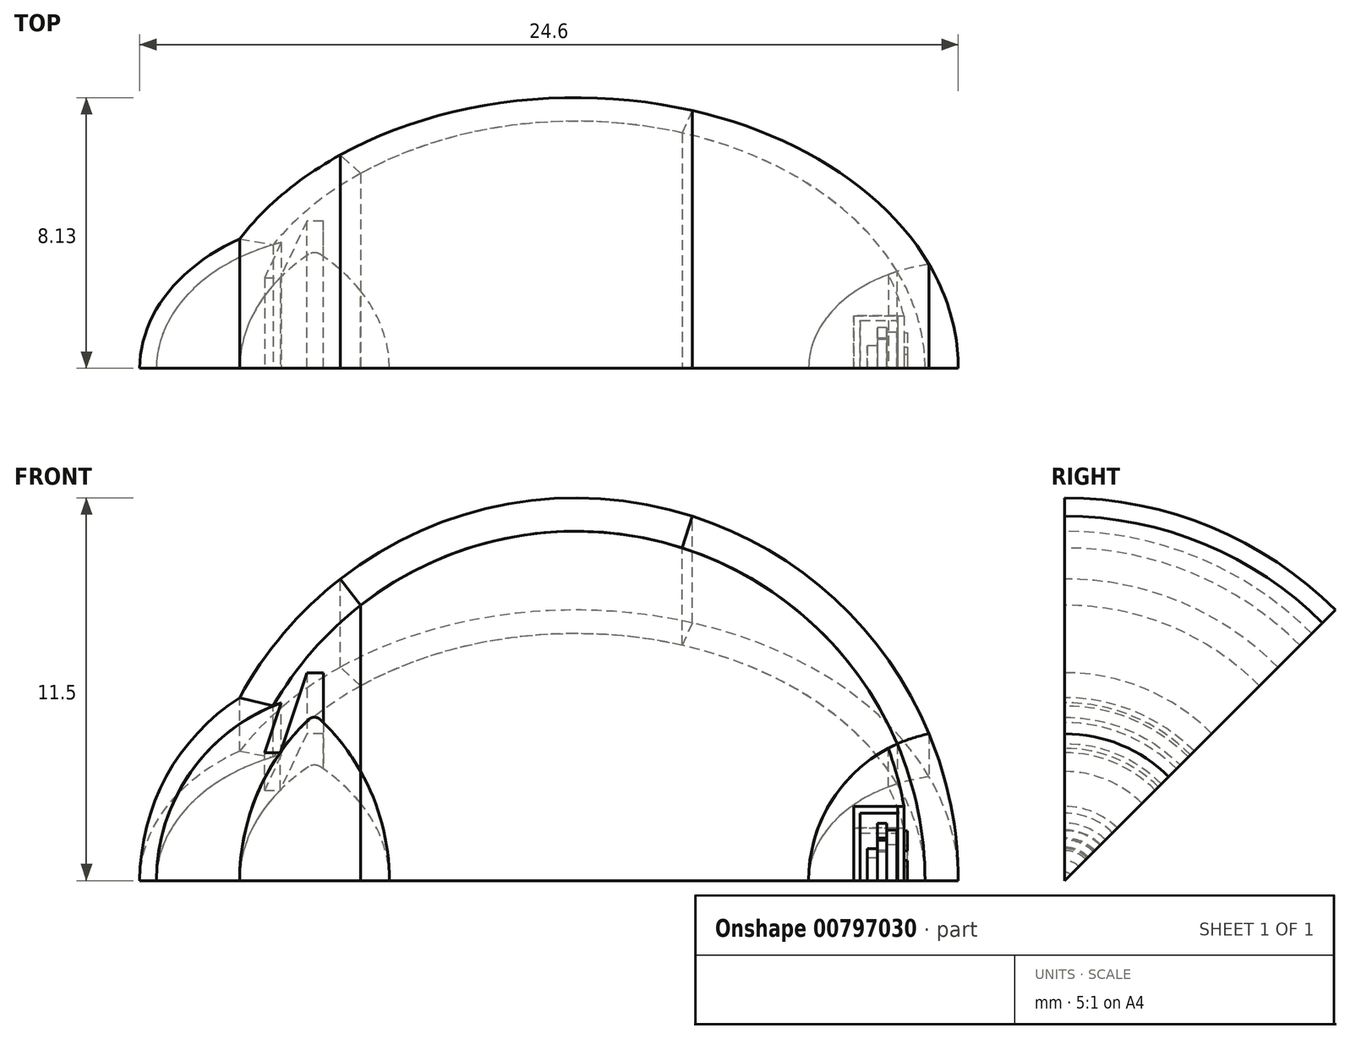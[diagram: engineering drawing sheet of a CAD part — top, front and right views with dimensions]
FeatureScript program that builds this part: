
annotation { "Feature Type Name" : "Feature", "Feature Type Description" : "" }
export const myFeature = defineFeature(function(context is Context, id is Id, definition is map)
    precondition{}
    {
        {
            var Q0;
            Q0=qCreatedBy(makeId("Front.planeOp"),FACE);
            var sketch = newSketch(context, id + "F0", { "sketchPlane" : qUnion([Q0])});
            skArc(sketch, "E0", {"start": v(11.5, 0) * mm, "mid": v(2.84, 11.14) * mm, "end": v(-10.1, 5.5) * mm});
            skLineSegment(sketch, "E1", {"start": v(11.5, 0) * mm, "end": v(-11.5, 0) * mm});
            skArc(sketch, "E2", {"start": v(-10.1, 5.5) * mm, "mid": v(-12.3, 3.13) * mm, "end": v(-13.1, 0) * mm});
            skLineSegment(sketch, "E3", {"start": v(-11.5, 0) * mm, "end": v(-13.1, 0) * mm});
            skSolve(sketch);
        }
        {
            var Q0;
            Q0=qSketchRegion(id+"F0",true);
            var Q1;
            Q1=sQuery(id+"F0.wireOp",EDGE,"E1");
            revolve(context, id + "F1", {"entities" : qUnion([Q0]), "axis" : qUnion([Q1]), "revolveType" : RevolveType.ONE_DIRECTION, "angle" : 45 * degree});
        }
        {
            var Q0;
            Q0=qCreatedBy(makeId("Front.planeOp"),FACE);
            var sketch = newSketch(context, id + "F2", { "sketchPlane" : qUnion([Q0])});
            skLineSegment(sketch, "E4", {"start": v(-10.1, 5.5) * mm, "end": v(-9.1, 5.25) * mm});
            skLineSegment(sketch, "E5", {"start": v(11.5, 0) * mm, "end": v(10.5, 0) * mm});
            skArc(sketch, "E6", {"start": v(10.5, 0) * mm, "mid": v(2.72, 10.14) * mm, "end": v(-9.1, 5.25) * mm});
            skArc(sketch, "E7", {"start": v(11.5, 0) * mm, "mid": v(2.84, 11.14) * mm, "end": v(-10.1, 5.5) * mm});
            skSolve(sketch);
        }
        {
            var Q0;
            Q0=makeQuery(id+"F2.imprint","IMPRINT",FACE,{"disambiguationData":[TD([[makeQuery(id+"F2.imprint","IMPRINT",EDGE,{"derivedFrom":sQuery(id+"F2.wireOp",EDGE,"E4")}),1.0]])]});
            var Q1;
            Q1=sQuery(id+"F2.wireOp",EDGE,"E6");
            var Q2;
            Q2=sQuery(id+"F2.wireOp",EDGE,"E4");
            var Q3;
            Q3=sQuery(id+"F0.wireOp",EDGE,"E1");
            revolve(context, id + "F3", {"operationType" : NewBodyOperationType.REMOVE, "entities" : qUnion([Q0]), "surfaceEntities" : qUnion([Q1, Q2]), "axis" : qUnion([Q3]), "revolveType" : RevolveType.ONE_DIRECTION, "angle" : 45 * degree});
        }
        {
            var Q0;
            Q0=qSketchRegion(id+"F2",true);
            var Q1;
            Q1=sQuery(id+"F0.wireOp",EDGE,"E1");
            revolve(context, id + "F4", {"entities" : qUnion([Q0]), "axis" : qUnion([Q1]), "revolveType" : RevolveType.ONE_DIRECTION, "angle" : 45 * degree});
        }
        {
            var Q0;
            Q0=makeQuery(id+"F0.imprint","IMPRINT",FACE,{"disambiguationData":[TD([[makeQuery(id+"F0.imprint","IMPRINT",EDGE,{"derivedFrom":sQuery(id+"F0.wireOp",EDGE,"E0")}),1.0]])]});
            var sketch = newSketch(context, id + "F5", { "sketchPlane" : qUnion([Q0])});
            skArc(sketch, "E8", {"start": v(-9.1, 5.25) * mm, "mid": v(-11.64, 3.16) * mm, "end": v(-12.6, 0) * mm});
            skLineSegment(sketch, "E9", {"start": v(-10.1, 5.5) * mm, "end": v(-9.1, 5.25) * mm});
            skLineSegment(sketch, "E10", {"start": v(-13.1, 0) * mm, "end": v(-12.6, 0) * mm});
            skArc(sketch, "E11", {"start": v(-10.1, 5.5) * mm, "mid": v(-12.3, 3.13) * mm, "end": v(-13.1, 0) * mm});
            skSolve(sketch);
        }
        {
            var Q0;
            Q0=qSketchRegion(id+"F5",true);
            var Q1;
            Q1=sQuery(id+"F5.wireOp",EDGE,"E8");
            var Q2;
            Q2=sQuery(id+"F5.wireOp",EDGE,"E9");
            var Q3;
            Q3=sQuery(id+"F0.wireOp",EDGE,"E3");
            revolve(context, id + "F6", {"operationType" : NewBodyOperationType.REMOVE, "entities" : qUnion([Q0]), "surfaceEntities" : qUnion([Q1, Q2]), "axis" : qUnion([Q3]), "revolveType" : RevolveType.ONE_DIRECTION, "angle" : 45 * degree});
        }
        {
            var Q0;
            Q0=qSketchRegion(id+"F5",true);
            var Q1;
            Q1=sQuery(id+"F0.wireOp",EDGE,"E1");
            revolve(context, id + "F7", {"entities" : qUnion([Q0]), "axis" : qUnion([Q1]), "revolveType" : RevolveType.ONE_DIRECTION, "angle" : 45 * degree});
        }
        {
            var Q0;
            Q0=qCreatedBy(makeId("Front.planeOp"),FACE);
            var sketch = newSketch(context, id + "F8", { "sketchPlane" : qUnion([Q0])});
            skArc(sketch, "E12", {"start": v(10, 0) * mm, "mid": v(8.28, 6.14) * mm, "end": v(3.2, 10) * mm});
            skLineSegment(sketch, "E13", {"start": v(10, 0) * mm, "end": v(10.5, 0) * mm});
            skArc(sketch, "E14", {"start": v(10.5, 0) * mm, "mid": v(8.48, 6.2) * mm, "end": v(3.2, 10) * mm});
            skSolve(sketch);
        }
        {
            var Q0;
            Q0=qSketchRegion(id+"F8",true);
            var Q1;
            Q1=sQuery(id+"F8.wireOp",EDGE,"E12");
            var Q2;
            Q2=sQuery(id+"F0.wireOp",EDGE,"E1");
            revolve(context, id + "F9", {"operationType" : NewBodyOperationType.REMOVE, "entities" : qUnion([Q0]), "surfaceEntities" : qUnion([Q1]), "axis" : qUnion([Q2]), "revolveType" : RevolveType.ONE_DIRECTION, "angle" : 45 * degree});
        }
        {
            var Q0;
            Q0=qSketchRegion(id+"F8",true);
            var Q1;
            Q1=sQuery(id+"F8.wireOp",EDGE,"E13");
            revolve(context, id + "F10", {"surfaceOperationType" : NewSurfaceOperationType.NEW, "entities" : qUnion([Q0]), "axis" : qUnion([Q1]), "revolveType" : RevolveType.ONE_DIRECTION, "oppositeDirection" : true, "angle" : 45 * degree});
        }
        {
            var Q0;
            Q0=makeQuery(id+"F0.imprint","IMPRINT",FACE,{"disambiguationData":[TD([[makeQuery(id+"F0.imprint","IMPRINT",EDGE,{"derivedFrom":sQuery(id+"F0.wireOp",EDGE,"E0")}),1.0]])]});
            var sketch = newSketch(context, id + "F11", { "sketchPlane" : qUnion([Q0])});
            skLineSegment(sketch, "E15", {"start": v(8.35, 0) * mm, "end": v(9.86, 0) * mm});
            skLineSegment(sketch, "E16", {"start": v(9.86, 0) * mm, "end": v(9.86, 2.23) * mm});
            skLineSegment(sketch, "E17", {"start": v(9.86, 2.23) * mm, "end": v(8.35, 2.23) * mm});
            skLineSegment(sketch, "E18", {"start": v(8.35, 2.23) * mm, "end": v(8.35, 0) * mm});
            skSolve(sketch);
        }
        {
            var Q0;
            Q0=qSketchRegion(id+"F11",true);
            var Q1;
            Q1=sQuery(id+"F11.wireOp",EDGE,"E15");
            revolve(context, id + "F12", {"operationType" : NewBodyOperationType.REMOVE, "entities" : qUnion([Q0]), "axis" : qUnion([Q1]), "revolveType" : RevolveType.ONE_DIRECTION, "oppositeDirection" : true, "angle" : 45 * degree});
        }
        {
            var Q0;
            Q0=qSketchRegion(id+"F11",true);
            var Q1;
            Q1=sQuery(id+"F0.wireOp",EDGE,"E1");
            revolve(context, id + "F13", {"entities" : qUnion([Q0]), "axis" : qUnion([Q1]), "revolveType" : RevolveType.ONE_DIRECTION, "angle" : 45 * degree});
        }
        {
            var Q0;
            Q0=qCreatedBy(makeId("Front.planeOp"),FACE);
            var sketch = newSketch(context, id + "F14", { "sketchPlane" : qUnion([Q0])});
            skLineSegment(sketch, "E19", {"start": v(9.86, 2.23) * mm, "end": v(9.86, 0) * mm});
            skLineSegment(sketch, "E20", {"start": v(9.86, 0) * mm, "end": v(10, 0) * mm});
            skArc(sketch, "E21", {"start": v(10, 0) * mm, "mid": v(10, 1.12) * mm, "end": v(9.86, 2.23) * mm});
            skSolve(sketch);
        }
        {
            var Q0;
            Q0=qSketchRegion(id+"F14",true);
            var Q1;
            Q1=sQuery(id+"F14.wireOp",EDGE,"E20");
            revolve(context, id + "F15", {"operationType" : NewBodyOperationType.REMOVE, "entities" : qUnion([Q0]), "axis" : qUnion([Q1]), "revolveType" : RevolveType.ONE_DIRECTION, "oppositeDirection" : true, "angle" : 45 * degree});
        }
        {
            var Q0;
            Q0=qSketchRegion(id+"F14",true);
            var Q1;
            Q1=sQuery(id+"F0.wireOp",EDGE,"E1");
            revolve(context, id + "F16", {"operationType" : NewBodyOperationType.ADD, "entities" : qUnion([Q0]), "axis" : qUnion([Q1]), "revolveType" : RevolveType.ONE_DIRECTION, "angle" : 45 * degree});
        }
        {
            var Q0;
            Q0=qCreatedBy(makeId("Front.planeOp"),FACE);
            var sketch = newSketch(context, id + "F17", { "sketchPlane" : qUnion([Q0])});
            skLineSegment(sketch, "E22", {"start": v(3.5, 10.95) * mm, "end": v(3.2, 10) * mm});
            skArc(sketch, "E23", {"start": v(10.5, 0) * mm, "mid": v(8.48, 6.2) * mm, "end": v(3.2, 10) * mm});
            skArc(sketch, "E24", {"start": v(11.5, 0) * mm, "mid": v(9.29, 6.78) * mm, "end": v(3.5, 10.95) * mm});
            skLineSegment(sketch, "E25", {"start": v(10.5, 0) * mm, "end": v(11.5, 0) * mm});
            skSolve(sketch);
        }
        {
            var Q0;
            Q0=qSketchRegion(id+"F17",true);
            var Q1;
            Q1=sQuery(id+"F17.wireOp",EDGE,"E25");
            revolve(context, id + "F18", {"operationType" : NewBodyOperationType.REMOVE, "entities" : qUnion([Q0]), "axis" : qUnion([Q1]), "revolveType" : RevolveType.FULL, "oppositeDirection" : true});
        }
        {
            var Q0;
            Q0=qSketchRegion(id+"F17",true);
            var Q1;
            Q1=sQuery(id+"F0.wireOp",EDGE,"E1");
            revolve(context, id + "F19", {"entities" : qUnion([Q0]), "axis" : qUnion([Q1]), "revolveType" : RevolveType.ONE_DIRECTION, "angle" : 45 * degree});
        }
        {
            var Q0;
            Q0=qCreatedBy(makeId("Front.planeOp"),FACE);
            var sketch = newSketch(context, id + "F20", { "sketchPlane" : qUnion([Q0])});
            skArc(sketch, "E26", {"start": v(-8.85, 5.34) * mm, "mid": v(-11.57, 3.26) * mm, "end": v(-12.6, 0) * mm});
            skLineSegment(sketch, "E27", {"start": v(-8.85, 5.34) * mm, "end": v(-9.35, 3.84) * mm});
            skLineSegment(sketch, "E28", {"start": v(-9.35, 3.84) * mm, "end": v(-8.85, 3.84) * mm});
            skLineSegment(sketch, "E29", {"start": v(-12.6, 0) * mm, "end": v(-8.85, 0) * mm});
            skLineSegment(sketch, "E30", {"start": v(-8.85, 3.84) * mm, "end": v(-8.85, 0) * mm});
            skSolve(sketch);
        }
        {
            var Q0;
            Q0=qSketchRegion(id+"F20",true);
            var Q1;
            Q1=sQuery(id+"F20.wireOp",EDGE,"E29");
            revolve(context, id + "F21", {"operationType" : NewBodyOperationType.REMOVE, "entities" : qUnion([Q0]), "axis" : qUnion([Q1]), "revolveType" : RevolveType.FULL, "oppositeDirection" : true});
        }
        {
            var Q0;
            Q0=qSketchRegion(id+"F20",true);
            var Q1;
            Q1=sQuery(id+"F0.wireOp",EDGE,"E1");
            revolve(context, id + "F22", {"entities" : qUnion([Q0]), "axis" : qUnion([Q1]), "revolveType" : RevolveType.ONE_DIRECTION, "angle" : 45 * degree});
        }
        {
            var Q0;
            Q0=qCreatedBy(makeId("Front.planeOp"),FACE);
            var sketch = newSketch(context, id + "F23", { "sketchPlane" : qUnion([Q0])});
            skLineSegment(sketch, "E31", {"start": v(-5.6, 0) * mm, "end": v(-10.1, 0) * mm});
            skArc(sketch, "E32", {"start": v(-8.02, 4.84) * mm, "mid": v(-9.56, 2.63) * mm, "end": v(-10.1, 0) * mm});
            skLineSegment(sketch, "E33", {"start": v(-8.1, 0) * mm, "end": v(-8.1, 4.77) * mm, "construction": true});
            skArc(sketch, "E34", {"start": v(-5.6, 0) * mm, "mid": v(-6.14, 2.63) * mm, "end": v(-7.68, 4.84) * mm});
            skPoint(sketch, "E35.visualSharp", {"position": v(-7.85, 5) * mm});
            skArc(sketch, "E35.filletArc", {"start": v(-7.68, 4.84) * mm, "mid": v(-7.85, 4.91) * mm, "end": v(-8.02, 4.84) * mm});
            skSolve(sketch);
        }
        {
            var Q0;
            Q0=qSketchRegion(id+"F23",true);
            var Q1;
            Q1=sQuery(id+"F0.wireOp",EDGE,"E1");
            revolve(context, id + "F24", {"operationType" : NewBodyOperationType.REMOVE, "entities" : qUnion([Q0]), "axis" : qUnion([Q1]), "revolveType" : RevolveType.FULL, "oppositeDirection" : true});
        }
        {
            var Q0;
            Q0=qSketchRegion(id+"F23",true);
            var Q1;
            Q1=sQuery(id+"F0.wireOp",EDGE,"E1");
            revolve(context, id + "F25", {"entities" : qUnion([Q0]), "axis" : qUnion([Q1]), "revolveType" : RevolveType.ONE_DIRECTION, "angle" : 45 * degree});
        }
        {
            var Q0;
            Q0=qCreatedBy(makeId("Front.planeOp"),FACE);
            var sketch = newSketch(context, id + "F26", { "sketchPlane" : qUnion([Q0])});
            skLineSegment(sketch, "E36", {"start": v(-9.35, 3.84) * mm, "end": v(-8.88, 3.84) * mm});
            skLineSegment(sketch, "E37", {"start": v(-8.88, 3.84) * mm, "end": v(-8.08, 6.25) * mm});
            skLineSegment(sketch, "E38", {"start": v(-8.08, 6.25) * mm, "end": v(-7.58, 6.25) * mm});
            skLineSegment(sketch, "E39", {"start": v(-7.58, 6.25) * mm, "end": v(-7.58, 4.75) * mm});
            skLineSegment(sketch, "E40", {"start": v(-6.46, 3.28) * mm, "end": v(-6.46, 8.28) * mm});
            skLineSegment(sketch, "E41", {"start": v(-9.35, 3.84) * mm, "end": v(-8.85, 5.34) * mm});
            skArc(sketch, "E42", {"start": v(-6.46, 8.28) * mm, "mid": v(-7.92, 6.9) * mm, "end": v(-9.1, 5.25) * mm});
            skArc(sketch, "E43", {"start": v(-8.85, 5.34) * mm, "mid": v(-8.97, 5.3) * mm, "end": v(-9.1, 5.25) * mm});
            skArc(sketch, "E44", {"start": v(-6.46, 3.28) * mm, "mid": v(-6.97, 4.05) * mm, "end": v(-7.58, 4.75) * mm});
            skSolve(sketch);
        }
        {
            var Q0;
            Q0=qSketchRegion(id+"F26",true);
            var Q1;
            Q1=sQuery(id+"F23.wireOp",EDGE,"E31");
            revolve(context, id + "F27", {"operationType" : NewBodyOperationType.REMOVE, "entities" : qUnion([Q0]), "axis" : qUnion([Q1]), "revolveType" : RevolveType.FULL, "oppositeDirection" : true});
        }
        {
            var Q0;
            Q0=qSketchRegion(id+"F26",true);
            var Q1;
            Q1=sQuery(id+"F23.wireOp",EDGE,"E31");
            revolve(context, id + "F28", {"entities" : qUnion([Q0]), "axis" : qUnion([Q1]), "revolveType" : RevolveType.ONE_DIRECTION, "angle" : 45 * degree});
        }
        {
            var Q0;
            Q0=qCreatedBy(makeId("Front.planeOp"),FACE);
            var sketch = newSketch(context, id + "F29", { "sketchPlane" : qUnion([Q0])});
            skLineSegment(sketch, "E45", {"start": v(-6.46, 8.28) * mm, "end": v(-7.07, 9.07) * mm});
            skArc(sketch, "E46", {"start": v(-7.07, 9.07) * mm, "mid": v(-8.77, 7.44) * mm, "end": v(-10.1, 5.5) * mm});
            skArc(sketch, "E47", {"start": v(-6.46, 8.28) * mm, "mid": v(-7.92, 6.9) * mm, "end": v(-9.1, 5.25) * mm});
            skPoint(sketch, "E47.second.point", {"position": v(-9.1, 5.25) * mm});
            skPoint(sketch, "E47.third.point", {"position": v(-6.46, 8.28) * mm});
            skLineSegment(sketch, "E48", {"start": v(-10.1, 5.5) * mm, "end": v(-9.1, 5.25) * mm});
            skSolve(sketch);
        }
        {
            var Q0;
            Q0=qSketchRegion(id+"F29",true);
            var Q1;
            Q1=sQuery(id+"F23.wireOp",EDGE,"E31");
            revolve(context, id + "F30", {"operationType" : NewBodyOperationType.REMOVE, "entities" : qUnion([Q0]), "axis" : qUnion([Q1]), "revolveType" : RevolveType.FULL, "oppositeDirection" : true});
        }
        {
            var Q0;
            Q0=qSketchRegion(id+"F29",true);
            var Q1;
            Q1=sQuery(id+"F23.wireOp",EDGE,"E31");
            revolve(context, id + "F31", {"entities" : qUnion([Q0]), "axis" : qUnion([Q1]), "revolveType" : RevolveType.ONE_DIRECTION, "angle" : 45 * degree});
        }
        {
            var Q0;
            Q0=qCreatedBy(makeId("Front.planeOp"),FACE);
            var sketch = newSketch(context, id + "F32", { "sketchPlane" : qUnion([Q0])});
            skLineSegment(sketch, "E49", {"start": v(-6.46, 0) * mm, "end": v(-5.6, 0) * mm});
            skLineSegment(sketch, "E50", {"start": v(-6.46, 0) * mm, "end": v(-6.46, 3.28) * mm});
            skArc(sketch, "E51", {"start": v(-5.6, 0) * mm, "mid": v(-5.82, 1.7) * mm, "end": v(-6.46, 3.28) * mm});
            skPoint(sketch, "E51.third.point", {"position": v(-5.6, 0) * mm});
            skSolve(sketch);
        }
        {
            var Q0;
            Q0=qSketchRegion(id+"F32",true);
            var Q1;
            Q1=sQuery(id+"F32.wireOp",EDGE,"E49");
            revolve(context, id + "F33", {"operationType" : NewBodyOperationType.REMOVE, "entities" : qUnion([Q0]), "axis" : qUnion([Q1]), "revolveType" : RevolveType.FULL, "oppositeDirection" : true});
        }
        {
            var Q0;
            Q0=qSketchRegion(id+"F32",true);
            var Q1;
            Q1=sQuery(id+"F23.wireOp",EDGE,"E31");
            revolve(context, id + "F34", {"entities" : qUnion([Q0]), "axis" : qUnion([Q1]), "revolveType" : RevolveType.ONE_DIRECTION, "angle" : 45 * degree});
        }
        {
            var Q0;
            Q0=makeQuery(id+"F0.imprint","IMPRINT",FACE,{"disambiguationData":[TD([[makeQuery(id+"F0.imprint","IMPRINT",EDGE,{"derivedFrom":sQuery(id+"F0.wireOp",EDGE,"E0")}),1.0]])]});
            var sketch = newSketch(context, id + "F35", { "sketchPlane" : qUnion([Q0])});
            skLineSegment(sketch, "E52", {"start": v(9.67, 0) * mm, "end": v(9.67, 2.23) * mm});
            skLineSegment(sketch, "E53", {"start": v(9.67, 2.23) * mm, "end": v(9.86, 2.23) * mm});
            skLineSegment(sketch, "E54", {"start": v(9.86, 2.23) * mm, "end": v(9.86, 0) * mm});
            skSolve(sketch);
        }
        {
            var Q0;
            {var subQ0=sQuery(id+"F35.wireOp",EDGE,"E52");Q0=makeQuery(id+"F35.imprint","IMPRINT",FACE,{"disambiguationData":[TD([[makeQuery(id+"F35.imprint","IMPRINT",EDGE,{"derivedFrom":subQ0}),-1.0]])]});}
            var Q1;
            Q1=sQuery(id+"F0.wireOp",EDGE,"E1");
            revolve(context, id + "F36", {"operationType" : NewBodyOperationType.REMOVE, "surfaceOperationType" : NewSurfaceOperationType.NEW, "entities" : qUnion([Q0]), "axis" : qUnion([Q1]), "revolveType" : RevolveType.ONE_DIRECTION, "angle" : 45 * degree});
        }
        {
            var Q0;
            Q0=makeQuery(id+"F0.imprint","IMPRINT",FACE,{"disambiguationData":[TD([[makeQuery(id+"F0.imprint","IMPRINT",EDGE,{"derivedFrom":sQuery(id+"F0.wireOp",EDGE,"E0")}),1.0]])]});
            var sketch = newSketch(context, id + "F37", { "sketchPlane" : qUnion([Q0])});
            skLineSegment(sketch, "E55.bottom", {"start": v(9.67, 2.23) * mm, "end": v(9.86, 2.23) * mm});
            skLineSegment(sketch, "E55.top", {"start": v(9.67, 0) * mm, "end": v(9.86, 0) * mm});
            skLineSegment(sketch, "E55.left", {"start": v(9.67, 2.23) * mm, "end": v(9.67, 0) * mm});
            skLineSegment(sketch, "E55.right", {"start": v(9.86, 2.23) * mm, "end": v(9.86, 0) * mm});
            skSolve(sketch);
        }
        {
            var Q0;
            Q0 = qSketchRegion(id + "F37", true);
            var Q1;
            Q1=sQuery(id+"F0.wireOp",EDGE,"E1");
            revolve(context, id + "F38", {"surfaceOperationType" : NewSurfaceOperationType.NEW, "entities" : qUnion([Q0]), "axis" : qUnion([Q1]), "revolveType" : RevolveType.ONE_DIRECTION, "angle" : 45 * degree});
        }
        {
            var Q0;
            Q0=makeQuery(id+"F0.imprint","IMPRINT",FACE,{"disambiguationData":[TD([[makeQuery(id+"F0.imprint","IMPRINT",EDGE,{"derivedFrom":sQuery(id+"F0.wireOp",EDGE,"E0")}),1.0]])]});
            var sketch = newSketch(context, id + "F39", { "sketchPlane" : qUnion([Q0])});
            skLineSegment(sketch, "E56", {"start": v(8.55, 0) * mm, "end": v(8.55, 2.03) * mm});
            skLineSegment(sketch, "E57", {"start": v(8.55, 2.03) * mm, "end": v(9.67, 2.03) * mm});
            skLineSegment(sketch, "E58", {"start": v(9.67, 2.03) * mm, "end": v(9.67, 2.23) * mm});
            skLineSegment(sketch, "E59", {"start": v(9.67, 2.23) * mm, "end": v(8.35, 2.23) * mm});
            skLineSegment(sketch, "E60", {"start": v(8.35, 2.23) * mm, "end": v(8.35, 0) * mm});
            skLineSegment(sketch, "E61", {"start": v(8.35, 0) * mm, "end": v(8.55, 0) * mm});
            skSolve(sketch);
        }
        {
            var Q0;
            Q0 = qSketchRegion(id + "F39", true);
            var Q1;
            Q1=sQuery(id+"F0.wireOp",EDGE,"E1");
            revolve(context, id + "F40", {"operationType" : NewBodyOperationType.REMOVE, "surfaceOperationType" : NewSurfaceOperationType.NEW, "entities" : qUnion([Q0]), "axis" : qUnion([Q1]), "revolveType" : RevolveType.ONE_DIRECTION, "angle" : 45 * degree});
        }
        {
            var Q0;
            Q0 = qSketchRegion(id + "F39", true);
            var Q1;
            Q1=sQuery(id+"F0.wireOp",EDGE,"E1");
            revolve(context, id + "F41", {"surfaceOperationType" : NewSurfaceOperationType.NEW, "entities" : qUnion([Q0]), "axis" : qUnion([Q1]), "revolveType" : RevolveType.ONE_DIRECTION, "angle" : 45 * degree});
        }
        {
            var Q0;
            Q0=makeQuery(id+"F0.imprint","IMPRINT",FACE,{"disambiguationData":[TD([[makeQuery(id+"F0.imprint","IMPRINT",EDGE,{"derivedFrom":sQuery(id+"F0.wireOp",EDGE,"E0")}),1.0]])]});
            var sketch = newSketch(context, id + "F42", { "sketchPlane" : qUnion([Q0])});
            skLineSegment(sketch, "E62.bottom", {"start": v(9.65, 0) * mm, "end": v(9.35, 0) * mm});
            skLineSegment(sketch, "E62.top", {"start": v(9.65, 1.52) * mm, "end": v(9.35, 1.52) * mm});
            skLineSegment(sketch, "E62.left", {"start": v(9.65, 0) * mm, "end": v(9.65, 1.52) * mm});
            skLineSegment(sketch, "E62.right", {"start": v(9.35, 0) * mm, "end": v(9.35, 1.52) * mm});
            skSolve(sketch);
        }
        {
            var Q0;
            Q0 = qSketchRegion(id + "F42", true);
            var Q1;
            Q1=sQuery(id+"F42.wireOp",EDGE,"E62.bottom");
            revolve(context, id + "F43", {"operationType" : NewBodyOperationType.REMOVE, "surfaceOperationType" : NewSurfaceOperationType.NEW, "entities" : qUnion([Q0]), "axis" : qUnion([Q1]), "revolveType" : RevolveType.FULL, "oppositeDirection" : true});
        }
        {
            var Q0;
            Q0 = qSketchRegion(id + "F42", true);
            var Q1;
            Q1=sQuery(id+"F0.wireOp",EDGE,"E1");
            revolve(context, id + "F44", {"surfaceOperationType" : NewSurfaceOperationType.NEW, "entities" : qUnion([Q0]), "axis" : qUnion([Q1]), "revolveType" : RevolveType.ONE_DIRECTION, "angle" : 45 * degree});
        }
        {
            var Q0;
            Q0=makeQuery(id+"F0.imprint","IMPRINT",FACE,{"disambiguationData":[TD([[makeQuery(id+"F0.imprint","IMPRINT",EDGE,{"derivedFrom":sQuery(id+"F0.wireOp",EDGE,"E0")}),1.0]])]});
            var sketch = newSketch(context, id + "F45", { "sketchPlane" : qUnion([Q0])});
            skLineSegment(sketch, "E63.bottom", {"start": v(9.35, 0) * mm, "end": v(9.07, 0) * mm});
            skLineSegment(sketch, "E63.top", {"start": v(9.35, 1.22) * mm, "end": v(9.07, 1.22) * mm});
            skLineSegment(sketch, "E63.left", {"start": v(9.35, 0) * mm, "end": v(9.35, 1.22) * mm});
            skLineSegment(sketch, "E63.right", {"start": v(9.07, 0) * mm, "end": v(9.07, 1.22) * mm});
            skSolve(sketch);
        }
        {
            var Q0;
            Q0 = qSketchRegion(id + "F45", true);
            var Q1;
            Q1=sQuery(id+"F45.wireOp",EDGE,"E63.bottom");
            revolve(context, id + "F46", {"operationType" : NewBodyOperationType.REMOVE, "surfaceOperationType" : NewSurfaceOperationType.NEW, "entities" : qUnion([Q0]), "axis" : qUnion([Q1]), "revolveType" : RevolveType.FULL, "oppositeDirection" : true});
        }
        {
            var Q0;
            Q0 = qSketchRegion(id + "F45", true);
            var Q1;
            Q1=sQuery(id+"F0.wireOp",EDGE,"E1");
            revolve(context, id + "F47", {"surfaceOperationType" : NewSurfaceOperationType.NEW, "entities" : qUnion([Q0]), "axis" : qUnion([Q1]), "revolveType" : RevolveType.ONE_DIRECTION, "angle" : 45 * degree});
        }
        {
            var Q0;
            Q0=makeQuery(id+"F0.imprint","IMPRINT",FACE,{"disambiguationData":[TD([[makeQuery(id+"F0.imprint","IMPRINT",EDGE,{"derivedFrom":sQuery(id+"F0.wireOp",EDGE,"E0")}),1.0]])]});
            var sketch = newSketch(context, id + "F48", { "sketchPlane" : qUnion([Q0])});
            skLineSegment(sketch, "E64.bottom", {"start": v(9.07, 0) * mm, "end": v(8.77, 0) * mm});
            skLineSegment(sketch, "E64.top", {"start": v(9.07, 0.96) * mm, "end": v(8.77, 0.96) * mm});
            skLineSegment(sketch, "E64.left", {"start": v(9.07, 0) * mm, "end": v(9.07, 0.96) * mm});
            skLineSegment(sketch, "E64.right", {"start": v(8.77, 0) * mm, "end": v(8.77, 0.96) * mm});
            skSolve(sketch);
        }
        {
            var Q0;
            Q0 = qSketchRegion(id + "F48", true);
            var Q1;
            Q1=sQuery(id+"F48.wireOp",EDGE,"E64.bottom");
            revolve(context, id + "F49", {"operationType" : NewBodyOperationType.REMOVE, "surfaceOperationType" : NewSurfaceOperationType.NEW, "entities" : qUnion([Q0]), "axis" : qUnion([Q1]), "revolveType" : RevolveType.FULL, "oppositeDirection" : true});
        }
        {
            var Q0;
            Q0 = qSketchRegion(id + "F48", true);
            var Q1;
            Q1=sQuery(id+"F0.wireOp",EDGE,"E1");
            revolve(context, id + "F50", {"surfaceOperationType" : NewSurfaceOperationType.NEW, "entities" : qUnion([Q0]), "axis" : qUnion([Q1]), "revolveType" : RevolveType.ONE_DIRECTION, "angle" : 45 * degree});
        }
        {
            var Q0;
            Q0=makeQuery(id+"F0.imprint","IMPRINT",FACE,{"disambiguationData":[TD([[makeQuery(id+"F0.imprint","IMPRINT",EDGE,{"derivedFrom":sQuery(id+"F0.wireOp",EDGE,"E0")}),1.0]])]});
            var sketch = newSketch(context, id + "F51", { "sketchPlane" : qUnion([Q0])});
            skLineSegment(sketch, "E65.bottom", {"start": v(9.35, 1.28) * mm, "end": v(9.07, 1.28) * mm});
            skLineSegment(sketch, "E65.top", {"start": v(9.35, 1.73) * mm, "end": v(9.07, 1.73) * mm});
            skLineSegment(sketch, "E65.left", {"start": v(9.35, 1.28) * mm, "end": v(9.35, 1.73) * mm});
            skLineSegment(sketch, "E65.right", {"start": v(9.07, 1.28) * mm, "end": v(9.07, 1.73) * mm});
            skSolve(sketch);
        }
        {
            var Q0;
            Q0 = qSketchRegion(id + "F51", true);
            var Q1;
            Q1=sQuery(id+"F0.wireOp",EDGE,"E1");
            revolve(context, id + "F52", {"operationType" : NewBodyOperationType.REMOVE, "surfaceOperationType" : NewSurfaceOperationType.NEW, "entities" : qUnion([Q0]), "axis" : qUnion([Q1]), "revolveType" : RevolveType.FULL, "oppositeDirection" : true});
        }
        {
            var Q0;
            Q0 = qSketchRegion(id + "F51", true);
            var Q1;
            Q1=sQuery(id+"F0.wireOp",EDGE,"E1");
            revolve(context, id + "F53", {"surfaceOperationType" : NewSurfaceOperationType.NEW, "entities" : qUnion([Q0]), "axis" : qUnion([Q1]), "revolveType" : RevolveType.ONE_DIRECTION, "angle" : 45 * degree});
        }
        {
            var Q0;
            Q0=makeQuery(id+"F0.imprint","IMPRINT",FACE,{"disambiguationData":[TD([[makeQuery(id+"F0.imprint","IMPRINT",EDGE,{"derivedFrom":sQuery(id+"F0.wireOp",EDGE,"E0")}),1.0]])]});
            var sketch = newSketch(context, id + "F54", { "sketchPlane" : qUnion([Q0])});
            skLineSegment(sketch, "E66.bottom", {"start": v(9.67, 0) * mm, "end": v(9.65, 0) * mm});
            skLineSegment(sketch, "E66.top", {"start": v(9.67, 0.25) * mm, "end": v(9.65, 0.25) * mm});
            skLineSegment(sketch, "E66.left", {"start": v(9.67, 0) * mm, "end": v(9.67, 0.25) * mm});
            skLineSegment(sketch, "E66.right", {"start": v(9.65, 0) * mm, "end": v(9.65, 0.25) * mm});
            skLineSegment(sketch, "E67.bottom", {"start": v(9.65, 1.25) * mm, "end": v(9.67, 1.25) * mm});
            skLineSegment(sketch, "E67.top", {"start": v(9.65, 1) * mm, "end": v(9.67, 1) * mm});
            skLineSegment(sketch, "E67.left", {"start": v(9.65, 1.25) * mm, "end": v(9.65, 1) * mm});
            skLineSegment(sketch, "E67.right", {"start": v(9.67, 1.25) * mm, "end": v(9.67, 1) * mm});
            skSolve(sketch);
        }
        {
            var Q0;
            Q0 = qSketchRegion(id + "F54", true);
            var Q1;
            Q1=sQuery(id+"F54.wireOp",EDGE,"E66.bottom");
            revolve(context, id + "F55", {"operationType" : NewBodyOperationType.REMOVE, "surfaceOperationType" : NewSurfaceOperationType.NEW, "entities" : qUnion([Q0]), "axis" : qUnion([Q1]), "revolveType" : RevolveType.FULL, "oppositeDirection" : true});
        }
        {
            var Q0;
            Q0 = qSketchRegion(id + "F54", true);
            var Q1;
            Q1=sQuery(id+"F0.wireOp",EDGE,"E1");
            revolve(context, id + "F56", {"surfaceOperationType" : NewSurfaceOperationType.NEW, "entities" : qUnion([Q0]), "axis" : qUnion([Q1]), "revolveType" : RevolveType.ONE_DIRECTION, "angle" : 45 * degree});
        }
        {
            var Q0;
            Q0=makeQuery(id+"F0.imprint","IMPRINT",FACE,{"disambiguationData":[TD([[makeQuery(id+"F0.imprint","IMPRINT",EDGE,{"derivedFrom":sQuery(id+"F0.wireOp",EDGE,"E0")}),1.0]])]});
            var sketch = newSketch(context, id + "F57", { "sketchPlane" : qUnion([Q0])});
            skLineSegment(sketch, "E68.bottom", {"start": v(9.86, 0.6) * mm, "end": v(9.96, 0.6) * mm});
            skLineSegment(sketch, "E68.top", {"start": v(9.86, 0) * mm, "end": v(9.96, 0) * mm});
            skLineSegment(sketch, "E68.left", {"start": v(9.86, 0.6) * mm, "end": v(9.86, 0) * mm});
            skLineSegment(sketch, "E68.right", {"start": v(9.96, 0.6) * mm, "end": v(9.96, 0) * mm});
            skLineSegment(sketch, "E69.bottom", {"start": v(9.86, 1.5) * mm, "end": v(9.96, 1.5) * mm});
            skLineSegment(sketch, "E69.top", {"start": v(9.86, 0.9) * mm, "end": v(9.96, 0.9) * mm});
            skLineSegment(sketch, "E69.left", {"start": v(9.86, 1.5) * mm, "end": v(9.86, 0.9) * mm});
            skLineSegment(sketch, "E69.right", {"start": v(9.96, 1.5) * mm, "end": v(9.96, 0.9) * mm});
            skSolve(sketch);
        }
        {
            var Q0;
            Q0 = qSketchRegion(id + "F57", true);
            var Q1;
            Q1=sQuery(id+"F57.wireOp",EDGE,"E68.top");
            revolve(context, id + "F58", {"operationType" : NewBodyOperationType.REMOVE, "surfaceOperationType" : NewSurfaceOperationType.NEW, "entities" : qUnion([Q0]), "axis" : qUnion([Q1]), "revolveType" : RevolveType.FULL, "oppositeDirection" : true});
        }
        {
            var Q0;
            Q0 = qSketchRegion(id + "F57", true);
            var Q1;
            Q1=sQuery(id+"F0.wireOp",EDGE,"E1");
            revolve(context, id + "F59", {"surfaceOperationType" : NewSurfaceOperationType.NEW, "entities" : qUnion([Q0]), "axis" : qUnion([Q1]), "revolveType" : RevolveType.ONE_DIRECTION, "angle" : 45 * degree});
        }
        {
            var Q0;
            Q0=makeQuery(id+"F0.imprint","IMPRINT",FACE,{"disambiguationData":[TD([[makeQuery(id+"F0.imprint","IMPRINT",EDGE,{"derivedFrom":sQuery(id+"F0.wireOp",EDGE,"E0")}),1.0]])]});
            var sketch = newSketch(context, id + "F60", { "sketchPlane" : qUnion([Q0])});
            skArc(sketch, "E70", {"start": v(9.4, 3.98) * mm, "mid": v(7.64, 2.32) * mm, "end": v(7, 0) * mm});
            skLineSegment(sketch, "E71", {"start": v(7, 0) * mm, "end": v(8.35, 0) * mm});
            skLineSegment(sketch, "E72", {"start": v(8.35, 0) * mm, "end": v(8.35, 2.23) * mm});
            skLineSegment(sketch, "E73", {"start": v(8.35, 2.23) * mm, "end": v(9.86, 2.23) * mm});
            skArc(sketch, "E74", {"start": v(9.86, 2.23) * mm, "mid": v(9.67, 3.11) * mm, "end": v(9.4, 3.98) * mm});
            skSolve(sketch);
        }
        {
            var Q0;
            Q0 = qSketchRegion(id + "F60", true);
            var Q1;
            Q1=sQuery(id+"F60.wireOp",EDGE,"E71");
            revolve(context, id + "F61", {"operationType" : NewBodyOperationType.REMOVE, "surfaceOperationType" : NewSurfaceOperationType.NEW, "entities" : qUnion([Q0]), "axis" : qUnion([Q1]), "revolveType" : RevolveType.FULL, "oppositeDirection" : true});
        }
        {
            var Q0;
            Q0 = qSketchRegion(id + "F60", true);
            var Q1;
            Q1=sQuery(id+"F0.wireOp",EDGE,"E1");
            revolve(context, id + "F62", {"surfaceOperationType" : NewSurfaceOperationType.NEW, "entities" : qUnion([Q0]), "axis" : qUnion([Q1]), "revolveType" : RevolveType.ONE_DIRECTION, "angle" : 45 * degree});
        }
        {
            var Q0;
            Q0=makeQuery(id+"F0.imprint","IMPRINT",FACE,{"disambiguationData":[TD([[makeQuery(id+"F0.imprint","IMPRINT",EDGE,{"derivedFrom":sQuery(id+"F0.wireOp",EDGE,"E0")}),1.0]])]});
            var sketch = newSketch(context, id + "F63", { "sketchPlane" : qUnion([Q0])});
            skArc(sketch, "E75", {"start": v(10.62, 4.41) * mm, "mid": v(10.13, 4.29) * mm, "end": v(9.66, 4.1) * mm});
            skLineSegment(sketch, "E76", {"start": v(11.5, 0) * mm, "end": v(10.5, 0) * mm});
            skArc(sketch, "E77", {"start": v(10.5, 0) * mm, "mid": v(10.29, 2.1) * mm, "end": v(9.66, 4.1) * mm});
            skArc(sketch, "E78", {"start": v(10.62, 4.41) * mm, "mid": v(11.28, 2.25) * mm, "end": v(11.5, 0) * mm});
            skSolve(sketch);
        }
        {
            var Q0;
            Q0 = qSketchRegion(id + "F63", true);
            var Q1;
            Q1=sQuery(id+"F63.wireOp",EDGE,"E76");
            revolve(context, id + "F64", {"operationType" : NewBodyOperationType.REMOVE, "surfaceOperationType" : NewSurfaceOperationType.NEW, "entities" : qUnion([Q0]), "axis" : qUnion([Q1]), "revolveType" : RevolveType.FULL, "oppositeDirection" : true});
        }
        {
            var Q0;
            Q0 = qSketchRegion(id + "F63", true);
            var Q1;
            Q1=sQuery(id+"F0.wireOp",EDGE,"E1");
            revolve(context, id + "F65", {"surfaceOperationType" : NewSurfaceOperationType.NEW, "entities" : qUnion([Q0]), "axis" : qUnion([Q1]), "revolveType" : RevolveType.ONE_DIRECTION, "angle" : 45 * degree});
        }
        {
            var Q0;
            Q0=makeQuery(id+"F0.imprint","IMPRINT",FACE,{"disambiguationData":[TD([[makeQuery(id+"F0.imprint","IMPRINT",EDGE,{"derivedFrom":sQuery(id+"F0.wireOp",EDGE,"E0")}),1.0]])]});
            var sketch = newSketch(context, id + "F66", { "sketchPlane" : qUnion([Q0])});
            skArc(sketch, "E79", {"start": v(9.66, 4.1) * mm, "mid": v(9.53, 4.04) * mm, "end": v(9.4, 3.98) * mm});
            skLineSegment(sketch, "E80", {"start": v(10.5, 0) * mm, "end": v(9.96, 0) * mm});
            skArc(sketch, "E81", {"start": v(10.5, 0) * mm, "mid": v(10.29, 2.1) * mm, "end": v(9.66, 4.1) * mm});
            skArc(sketch, "E82", {"start": v(9.86, 2.23) * mm, "mid": v(9.67, 3.11) * mm, "end": v(9.4, 3.98) * mm});
            skLineSegment(sketch, "E83", {"start": v(9.86, 2.23) * mm, "end": v(9.86, 1.5) * mm});
            skLineSegment(sketch, "E84", {"start": v(9.86, 1.5) * mm, "end": v(9.96, 1.5) * mm});
            skLineSegment(sketch, "E85", {"start": v(9.96, 1.5) * mm, "end": v(9.96, 0.9) * mm});
            skLineSegment(sketch, "E86", {"start": v(9.96, 0.9) * mm, "end": v(9.86, 0.9) * mm});
            skLineSegment(sketch, "E87", {"start": v(9.86, 0.9) * mm, "end": v(9.86, 0.6) * mm});
            skLineSegment(sketch, "E88", {"start": v(9.86, 0.6) * mm, "end": v(9.96, 0.6) * mm});
            skLineSegment(sketch, "E89", {"start": v(9.96, 0.6) * mm, "end": v(9.96, 0) * mm});
            skSolve(sketch);
        }
        {
            var Q0;
            Q0 = qSketchRegion(id + "F66", true);
            var Q1;
            Q1=sQuery(id+"F66.wireOp",EDGE,"E80");
            revolve(context, id + "F67", {"operationType" : NewBodyOperationType.REMOVE, "surfaceOperationType" : NewSurfaceOperationType.NEW, "entities" : qUnion([Q0]), "axis" : qUnion([Q1]), "revolveType" : RevolveType.FULL, "oppositeDirection" : true});
        }
        {
            var Q0;
            Q0 = qSketchRegion(id + "F66", true);
            var Q1;
            Q1=sQuery(id+"F0.wireOp",EDGE,"E1");
            revolve(context, id + "F68", {"surfaceOperationType" : NewSurfaceOperationType.NEW, "entities" : qUnion([Q0]), "axis" : qUnion([Q1]), "revolveType" : RevolveType.ONE_DIRECTION, "angle" : 45 * degree});
        }
        {
            var Q0;
            Q0=makeQuery(id+"F0.imprint","IMPRINT",FACE,{"disambiguationData":[TD([[makeQuery(id+"F0.imprint","IMPRINT",EDGE,{"derivedFrom":sQuery(id+"F0.wireOp",EDGE,"E0")}),1.0]])]});
            var sketch = newSketch(context, id + "F69", { "sketchPlane" : qUnion([Q0])});
            skLineSegment(sketch, "E90.bottom", {"start": v(9.35, 1.28) * mm, "end": v(9.07, 1.28) * mm});
            skLineSegment(sketch, "E90.top", {"start": v(9.35, 1.22) * mm, "end": v(9.07, 1.22) * mm});
            skLineSegment(sketch, "E90.left", {"start": v(9.35, 1.28) * mm, "end": v(9.35, 1.22) * mm});
            skLineSegment(sketch, "E90.right", {"start": v(9.07, 1.28) * mm, "end": v(9.07, 1.22) * mm});
            skSolve(sketch);
        }
        {
            var Q0;
            Q0 = qSketchRegion(id + "F69", true);
            var Q1;
            Q1=sQuery(id+"F0.wireOp",EDGE,"E1");
            revolve(context, id + "F70", {"operationType" : NewBodyOperationType.REMOVE, "surfaceOperationType" : NewSurfaceOperationType.NEW, "entities" : qUnion([Q0]), "axis" : qUnion([Q1]), "revolveType" : RevolveType.FULL, "oppositeDirection" : true});
        }
        {
            var Q0;
            Q0 = qSketchRegion(id + "F69", true);
            var Q1;
            Q1=sQuery(id+"F0.wireOp",EDGE,"E1");
            revolve(context, id + "F71", {"surfaceOperationType" : NewSurfaceOperationType.NEW, "entities" : qUnion([Q0]), "axis" : qUnion([Q1]), "revolveType" : RevolveType.ONE_DIRECTION, "angle" : 45 * degree});
        }
    });
